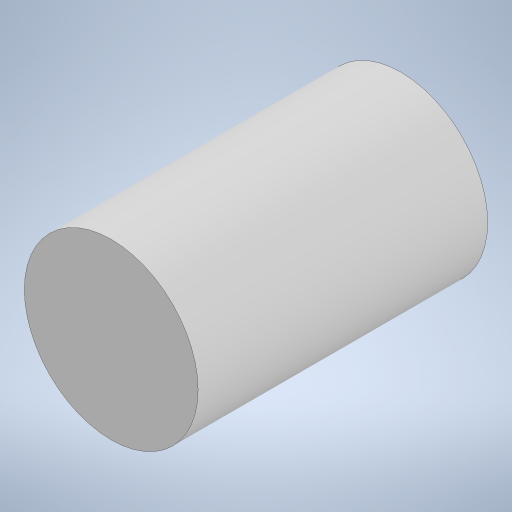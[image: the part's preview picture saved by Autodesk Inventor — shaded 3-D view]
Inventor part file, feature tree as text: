
AUTODESK INVENTOR PART (.ipt)
format: ipt  version: 2023 (Build 270158000, 158)  size: 244,224 bytes
history: native  units: mm
features: extrude x1, sketch x1
ambient origin geometry x8: Origin, YZ Plane, XZ Plane, XY Plane, X Axis, Y Axis, Z Axis, Center Point
bodies: Body1 (feature_tree)
feature tree (2):
  extrude  "Extrusion20"  Depth=15.0mm TaperAngle=0.0deg
  sketch  "Sketch25"  dims[d81=9.0mm d82=15.0mm d83=0.0mm d79=0.0mm d80=0.0mm]
